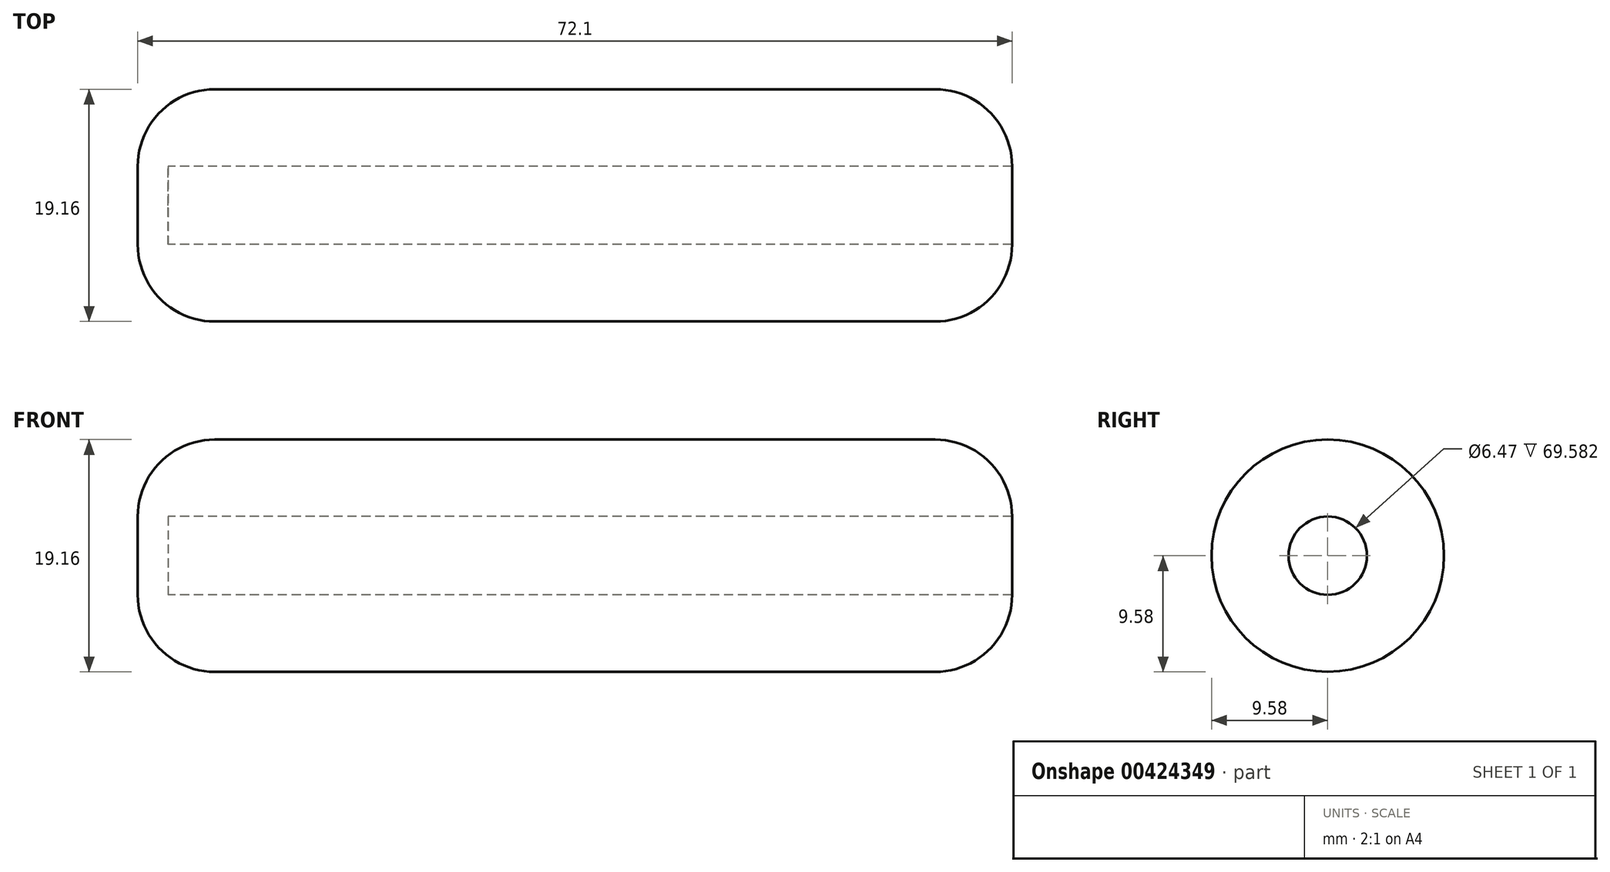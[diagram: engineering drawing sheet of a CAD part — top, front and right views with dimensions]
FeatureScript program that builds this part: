
annotation { "Feature Type Name" : "Feature", "Feature Type Description" : "" }
export const myFeature = defineFeature(function(context is Context, id is Id, definition is map)
    precondition{}
    {
        {
            var Q0;
            Q0=qCreatedBy(makeId("Front.planeOp"),FACE);
            var sketch = newSketch(context, id + "F0", { "sketchPlane" : qUnion([Q0])});
            skLineSegment(sketch, "E0", {"start": v(0, 0) * mm, "end": v(0, -9.58) * mm});
            skLineSegment(sketch, "E1", {"start": v(0, -9.58) * mm, "end": v(72.1, -9.58) * mm});
            skLineSegment(sketch, "E2", {"start": v(72.1, -9.58) * mm, "end": v(72.1, -3.23) * mm});
            skLineSegment(sketch, "E3", {"start": v(72.1, -3.23) * mm, "end": v(2.52, -3.23) * mm});
            skLineSegment(sketch, "E4", {"start": v(2.52, -3.23) * mm, "end": v(2.52, 0) * mm});
            skLineSegment(sketch, "E5", {"start": v(0, 0) * mm, "end": v(2.52, 0) * mm});
            skLineSegment(sketch, "E6", {"start": v(0, 0) * mm, "end": v(0, 6.48) * mm});
            skLineSegment(sketch, "E7", {"start": v(0, 6.48) * mm, "end": v(70.78, 6.48) * mm, "construction": true});
            skSolve(sketch);
        }
        {
            var Q0;
            Q0=qCreatedBy(makeId("Front.planeOp"),FACE);
            var sketch = newSketch(context, id + "F1", { "sketchPlane" : qUnion([Q0])});
            skLineSegment(sketch, "E8", {"start": v(0, 0) * mm, "end": v(0, -10.05) * mm});
            skLineSegment(sketch, "E9", {"start": v(0, 0) * mm, "end": v(64.84, 0) * mm});
            skSolve(sketch);
        }
        {
            var Q0;
            Q0=makeQuery(id+"F0.imprint","IMPRINT",FACE,{"disambiguationData":[TD([[makeQuery(id+"F0.imprint","IMPRINT",EDGE,{"derivedFrom":sQuery(id+"F0.wireOp",EDGE,"E0")}),1.0]])]});
            var Q1;
            Q1=sQuery(id+"F1.wireOp",EDGE,"E9");
            revolve(context, id + "F2", {"entities" : qUnion([Q0]), "axis" : qUnion([Q1]), "revolveType" : RevolveType.FULL});
        }
        {
            var Q0;
            Q0=makeQuery(id+"F2.opRevolve","SWEPT_EDGE",EDGE,{"disambiguationData":[OSD([sQuery(id+"F0.wireOp",EDGE,"E0"),sQuery(id+"F0.wireOp",EDGE,"E1")])]});
            var Q1;
            Q1=makeQuery(id+"F2.opRevolve","SWEPT_EDGE",EDGE,{"disambiguationData":[OSD([sQuery(id+"F0.wireOp",EDGE,"E1"),sQuery(id+"F0.wireOp",EDGE,"E2")])]});
            fillet(context, id + "F3", {"entities" : qUnion([Q0, Q1]), "radius" : 6.35 * mm, "tangentPropagation" : true, "allowEdgeOverflow" : false});
        }
    });
